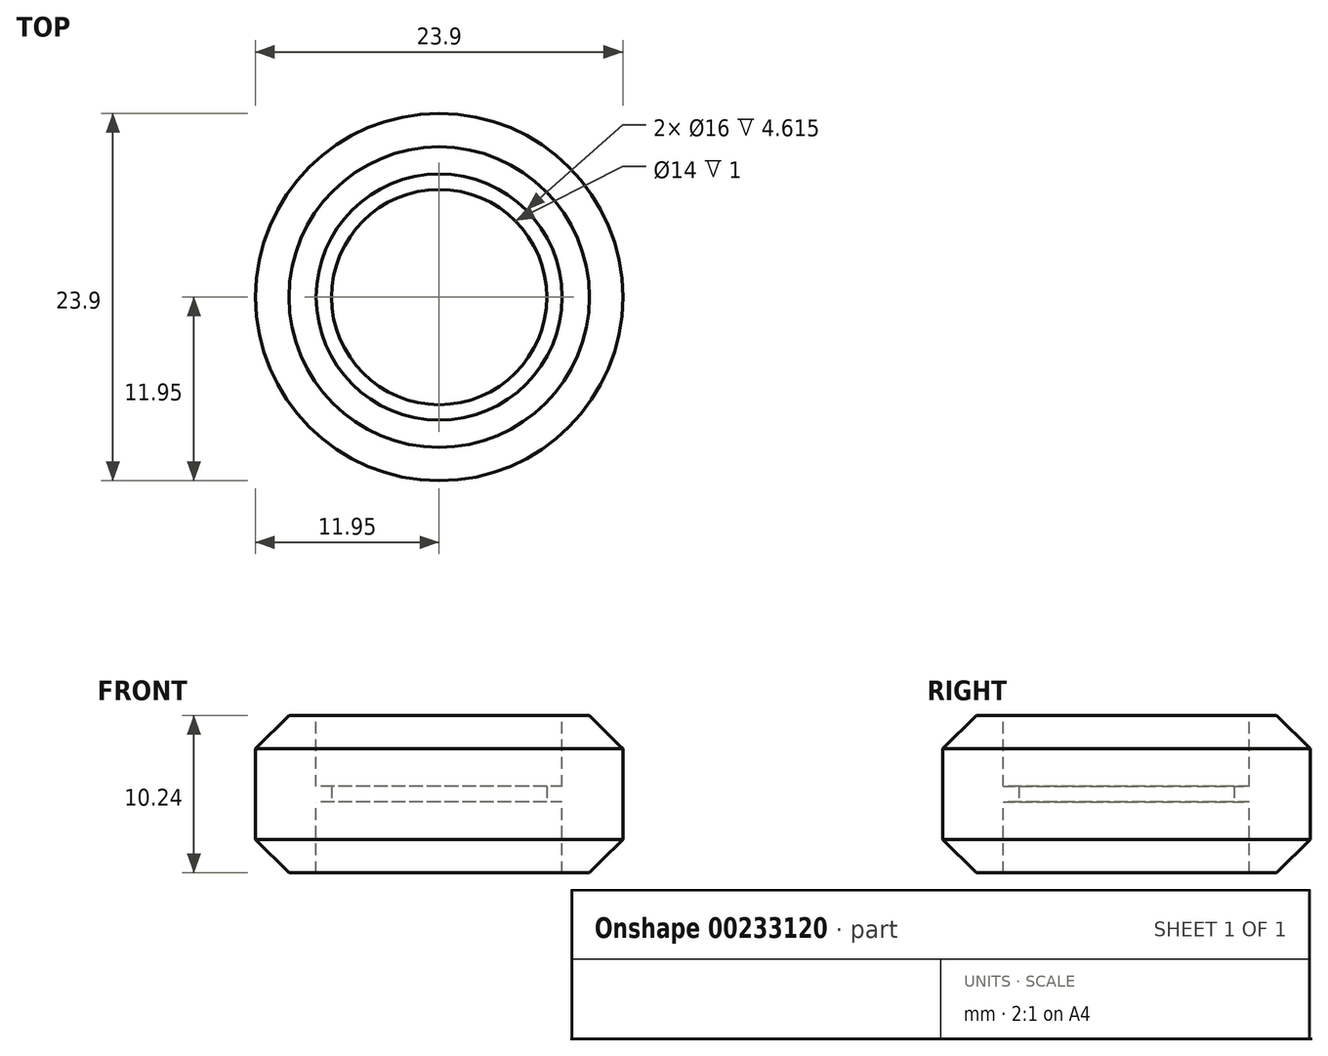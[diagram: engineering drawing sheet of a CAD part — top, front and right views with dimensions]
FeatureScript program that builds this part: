
annotation { "Feature Type Name" : "Feature", "Feature Type Description" : "" }
export const myFeature = defineFeature(function(context is Context, id is Id, definition is map)
    precondition{}
    {
        {
            var Q0;
            Q0=qCreatedBy(makeId("Front.planeOp"),FACE);
            var sketch = newSketch(context, id + "F0", { "sketchPlane" : qUnion([Q0])});
            skLineSegment(sketch, "E0.bottom", {"start": v(0, 5.11) * mm, "end": v(9.77, 5.11) * mm});
            skLineSegment(sketch, "E0.top", {"start": v(0, -5.11) * mm, "end": v(9.77, -5.11) * mm});
            skLineSegment(sketch, "E0.left", {"start": v(0, 5.11) * mm, "end": v(0, -5.11) * mm});
            skLineSegment(sketch, "E0.right", {"start": v(9.77, 5.11) * mm, "end": v(9.77, -5.11) * mm, "construction": true});
            skLineSegment(sketch, "E1", {"start": v(9.77, 5.11) * mm, "end": v(11.94, 2.94) * mm});
            skLineSegment(sketch, "E2", {"start": v(11.95, 2.94) * mm, "end": v(11.95, -2.94) * mm});
            skLineSegment(sketch, "E3", {"start": v(11.94, -2.94) * mm, "end": v(9.77, -5.11) * mm});
            skSolve(sketch);
        }
        {
            var Q0;
            Q0=makeQuery(id+"F0.imprint","IMPRINT",FACE,{"disambiguationData":[TD([[makeQuery(id+"F0.imprint","IMPRINT",EDGE,{"derivedFrom":sQuery(id+"F0.wireOp",EDGE,"E0.bottom")}),-1.0]])]});
            var Q1;
            Q1=sQuery(id+"F0.wireOp",EDGE,"E0.left");
            revolve(context, id + "F1", {"entities" : qUnion([Q0]), "axis" : qUnion([Q1]), "revolveType" : RevolveType.FULL});
        }
        {
            var Q0;
            Q0=qCreatedBy(makeId("Top.planeOp"),FACE);
            var sketch = newSketch(context, id + "F2", { "sketchPlane" : qUnion([Q0])});
            skCircle(sketch, "E4", {"center": v(0, 0) * mm, "radius": 8 * mm});
            skSolve(sketch);
        }
        {
            var Q0;
            Q0 = qSketchRegion(id + "F2", true);
            extrude(context, id + "F3", {"entities" : qUnion([Q0]), "operationType" : NewBodyOperationType.REMOVE, "endBound" : BoundingType.THROUGH_ALL, "oppositeDirection" : true, "depth" : 25 * mm, "hasSecondDirection" : true, "secondDirectionBound" : BoundingType.THROUGH_ALL, "secondDirectionOppositeDirection" : false, "secondDirectionDepth" : 25 * mm});
        }
        {
            var Q0;
            Q0=qCreatedBy(makeId("Top.planeOp"),FACE);
            var sketch = newSketch(context, id + "F4", { "sketchPlane" : qUnion([Q0])});
            skCircle(sketch, "E5", {"center": v(0, 0) * mm, "radius": 7 * mm});
            skCircle(sketch, "E6.0", {"center": v(0, 0) * mm, "radius": 8 * mm});
            skSolve(sketch);
        }
        {
            var Q0;
            Q0 = qSketchRegion(id + "F4", true);
            extrude(context, id + "F5", {"entities" : qUnion([Q0]), "operationType" : NewBodyOperationType.ADD, "depth" : 1 * mm, "symmetric" : true});
        }
    });
